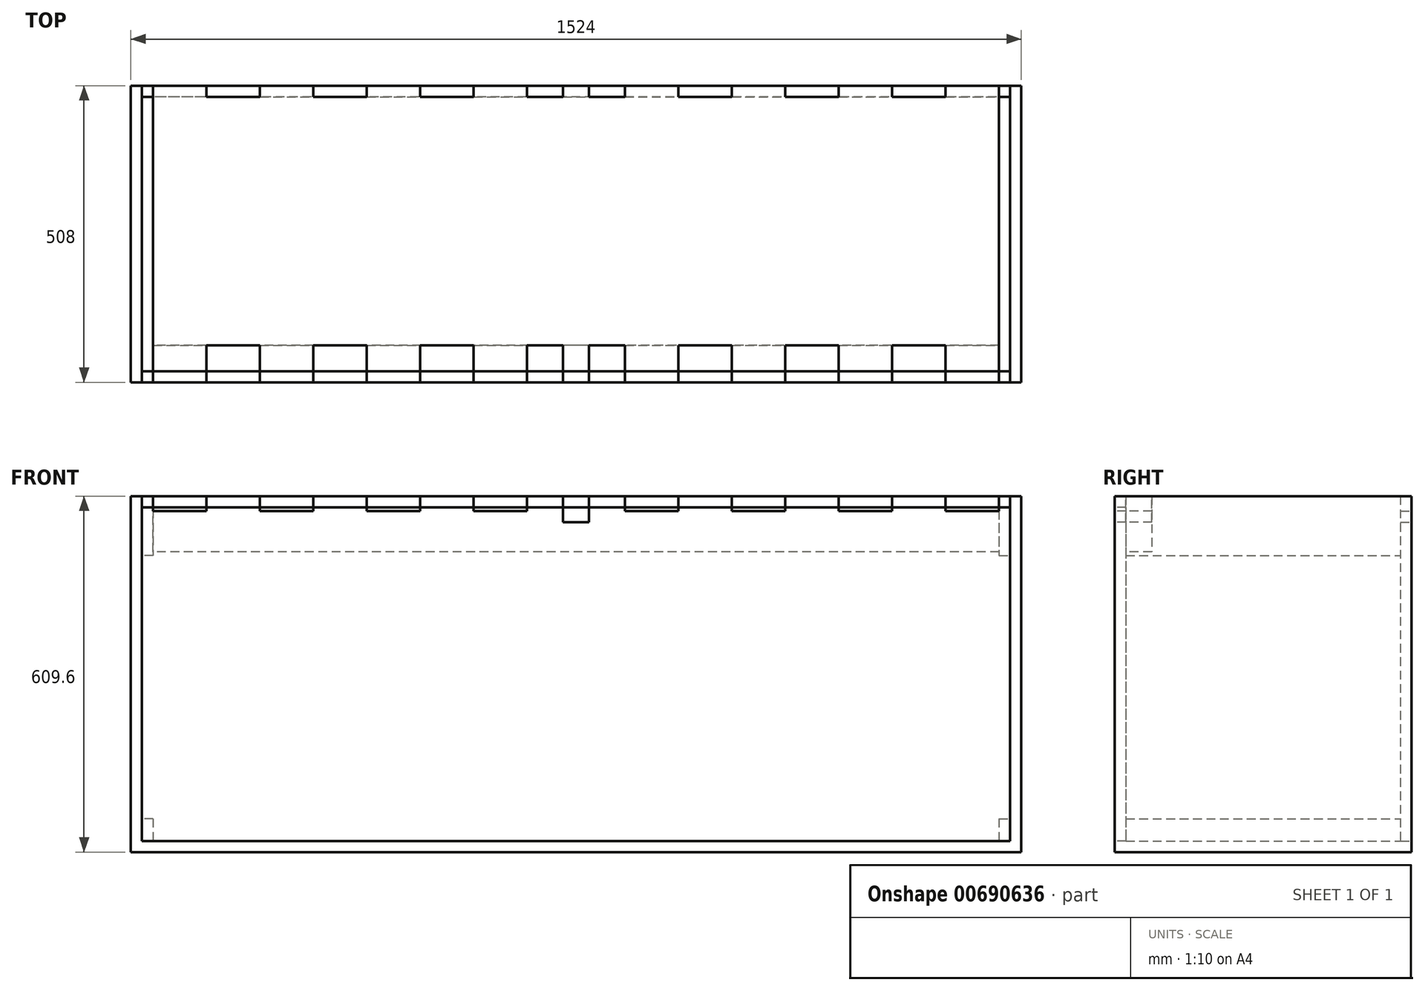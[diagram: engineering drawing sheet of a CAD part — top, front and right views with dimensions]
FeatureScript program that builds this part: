
annotation { "Feature Type Name" : "Feature", "Feature Type Description" : "" }
export const myFeature = defineFeature(function(context is Context, id is Id, definition is map)
    precondition{}
    {
        {
            var Q0;
            Q0=qCreatedBy(makeId("Top.planeOp"),FACE);
            var sketch = newSketch(context, id + "F0", { "sketchPlane" : qUnion([Q0])});
            skLineSegment(sketch, "E0.bottom", {"start": v(-762, -254) * mm, "end": v(762, -254) * mm});
            skLineSegment(sketch, "E0.top", {"start": v(-762, 254) * mm, "end": v(762, 254) * mm});
            skLineSegment(sketch, "E0.left", {"start": v(-762, -254) * mm, "end": v(-762, 254) * mm});
            skLineSegment(sketch, "E0.right", {"start": v(762, -254) * mm, "end": v(762, 254) * mm});
            skPoint(sketch, "E0.middle", {"position": v(0, 0) * mm});
            skSolve(sketch);
        }
        {
            var Q0;
            Q0=makeQuery(id+"F0.imprint","IMPRINT",FACE,{"disambiguationData":[TD([[makeQuery(id+"F0.imprint","IMPRINT",EDGE,{"derivedFrom":sQuery(id+"F0.wireOp",EDGE,"E0.bottom")}),1.0]])]});
            extrude(context, id + "F1", {"entities" : qUnion([Q0]), "oppositeDirection" : true, "depth" : 609.6 * mm, "offsetDistance" : 25.4 * mm});
        }
        {
            var Q0;
            Q0=makeQuery(id+"F1.opExtrude","SWEPT_FACE",FACE,{"disambiguationData":[OSD([sQuery(id+"F0.wireOp",EDGE,"E0.bottom")])]});
            var sketch = newSketch(context, id + "F2", { "sketchPlane" : qUnion([Q0])});
            skLineSegment(sketch, "E1.bottom", {"start": v(-742.95, -19.05) * mm, "end": v(742.95, -19.05) * mm});
            skLineSegment(sketch, "E1.top", {"start": v(-742.95, -590.55) * mm, "end": v(742.95, -590.55) * mm});
            skLineSegment(sketch, "E1.left", {"start": v(-742.95, -19.05) * mm, "end": v(-742.95, -590.55) * mm});
            skLineSegment(sketch, "E1.right", {"start": v(742.95, -19.05) * mm, "end": v(742.95, -590.55) * mm});
            skSolve(sketch);
        }
        {
            var Q0;
            Q0=qSketchRegion(id+"F2",true);
            extrude(context, id + "F3", {"entities" : qUnion([Q0]), "oppositeDirection" : true, "depth" : 19.05 * mm, "offsetDistance" : 25.4 * mm});
        }
        {
            var Q0;
            Q0=makeQuery(id+"F3.opExtrude","CAP_FACE",FACE,{"disambiguationData":[OSD([sQuery(id+"F2.wireOp",EDGE,"E1.bottom"),sQuery(id+"F2.wireOp",EDGE,"E1.top"),sQuery(id+"F2.wireOp",EDGE,"E1.left"),sQuery(id+"F2.wireOp",EDGE,"E1.right")])],"isStart":false});
            var sketch = newSketch(context, id + "F4", { "sketchPlane" : qUnion([Q0])});
            skLineSegment(sketch, "E2", {"start": v(-723.9, -95.25) * mm, "end": v(723.9, -95.25) * mm});
            skLineSegment(sketch, "E3", {"start": v(723.9, -95.25) * mm, "end": v(723.9, -25.4) * mm});
            skLineSegment(sketch, "E4", {"start": v(723.9, -25.4) * mm, "end": v(632.46, -25.4) * mm});
            skLineSegment(sketch, "E5", {"start": v(632.46, -25.4) * mm, "end": v(632.46, 0) * mm});
            skLineSegment(sketch, "E6", {"start": v(632.46, 0) * mm, "end": v(541.02, 0) * mm});
            skLineSegment(sketch, "E7", {"start": v(541.02, 0) * mm, "end": v(541.02, -25.4) * mm});
            skLineSegment(sketch, "E8", {"start": v(541.02, -25.4) * mm, "end": v(449.58, -25.4) * mm});
            skLineSegment(sketch, "E9", {"start": v(449.58, -25.4) * mm, "end": v(449.58, 0) * mm});
            skLineSegment(sketch, "E10", {"start": v(449.58, 0) * mm, "end": v(358.14, 0) * mm});
            skLineSegment(sketch, "E11", {"start": v(358.14, 0) * mm, "end": v(358.14, -25.4) * mm});
            skLineSegment(sketch, "E12", {"start": v(358.14, -25.4) * mm, "end": v(266.7, -25.4) * mm});
            skLineSegment(sketch, "E13", {"start": v(266.7, -25.4) * mm, "end": v(266.7, 0) * mm});
            skLineSegment(sketch, "E14", {"start": v(266.7, 0) * mm, "end": v(175.26, 0) * mm});
            skLineSegment(sketch, "E15", {"start": v(175.26, 0) * mm, "end": v(175.26, -25.4) * mm});
            skLineSegment(sketch, "E16", {"start": v(175.26, -25.4) * mm, "end": v(83.82, -25.4) * mm});
            skLineSegment(sketch, "E17", {"start": v(83.82, -25.4) * mm, "end": v(83.82, 0) * mm});
            skLineSegment(sketch, "E18", {"start": v(-83.82, 0) * mm, "end": v(-83.82, -25.4) * mm});
            skLineSegment(sketch, "E19", {"start": v(-83.82, -25.4) * mm, "end": v(-175.26, -25.4) * mm});
            skLineSegment(sketch, "E20", {"start": v(-175.26, -25.4) * mm, "end": v(-175.26, 0) * mm});
            skLineSegment(sketch, "E21", {"start": v(-175.26, 0) * mm, "end": v(-266.7, 0) * mm});
            skLineSegment(sketch, "E22", {"start": v(-266.7, 0) * mm, "end": v(-266.7, -25.4) * mm});
            skLineSegment(sketch, "E23", {"start": v(-266.7, -25.4) * mm, "end": v(-358.14, -25.4) * mm});
            skLineSegment(sketch, "E24", {"start": v(-358.14, -25.4) * mm, "end": v(-358.14, 0) * mm});
            skLineSegment(sketch, "E25", {"start": v(-358.14, 0) * mm, "end": v(-449.58, 0) * mm});
            skLineSegment(sketch, "E26", {"start": v(-449.58, 0) * mm, "end": v(-449.58, -25.4) * mm});
            skLineSegment(sketch, "E27", {"start": v(-449.58, -25.4) * mm, "end": v(-541.02, -25.4) * mm});
            skLineSegment(sketch, "E28", {"start": v(-541.02, -25.4) * mm, "end": v(-541.02, 0) * mm});
            skLineSegment(sketch, "E29", {"start": v(-541.02, 0) * mm, "end": v(-632.46, 0) * mm});
            skLineSegment(sketch, "E30", {"start": v(-632.46, 0) * mm, "end": v(-632.46, -25.4) * mm});
            skLineSegment(sketch, "E31", {"start": v(-632.46, -25.4) * mm, "end": v(-723.9, -25.4) * mm});
            skLineSegment(sketch, "E32", {"start": v(-723.9, -25.4) * mm, "end": v(-723.9, -95.25) * mm});
            skLineSegment(sketch, "E33", {"start": v(-83.82, 0) * mm, "end": v(-22.22, 0) * mm});
            skLineSegment(sketch, "E34", {"start": v(-22.22, 0) * mm, "end": v(-22.22, -44.45) * mm});
            skLineSegment(sketch, "E35", {"start": v(-22.22, -44.45) * mm, "end": v(22.23, -44.45) * mm});
            skLineSegment(sketch, "E36", {"start": v(22.23, -44.45) * mm, "end": v(22.23, 0) * mm});
            skLineSegment(sketch, "E37", {"start": v(22.23, 0) * mm, "end": v(83.82, 0) * mm});
            skSolve(sketch);
        }
        {
            var Q0;
            Q0=qSketchRegion(id+"F4",true);
            extrude(context, id + "F5", {"entities" : qUnion([Q0]), "depth" : 44.45 * mm, "offsetDistance" : 25.4 * mm});
        }
        {
            var Q0;
            Q0=makeQuery(id+"F1.opExtrude","SWEPT_FACE",FACE,{"disambiguationData":[OSD([sQuery(id+"F0.wireOp",EDGE,"E0.top")])]});
            var sketch = newSketch(context, id + "F6", { "sketchPlane" : qUnion([Q0])});
            skLineSegment(sketch, "E38", {"start": v(-742.95, -590.55) * mm, "end": v(742.95, -590.55) * mm});
            skLineSegment(sketch, "E39", {"start": v(742.95, -590.55) * mm, "end": v(742.95, 0) * mm});
            skLineSegment(sketch, "E40", {"start": v(632.46, -25.4) * mm, "end": v(632.46, 0) * mm});
            skLineSegment(sketch, "E41", {"start": v(632.46, 0) * mm, "end": v(541.02, 0) * mm});
            skLineSegment(sketch, "E42", {"start": v(541.02, 0) * mm, "end": v(541.02, -25.4) * mm});
            skLineSegment(sketch, "E43", {"start": v(541.02, -25.4) * mm, "end": v(449.58, -25.4) * mm});
            skLineSegment(sketch, "E44", {"start": v(449.58, -25.4) * mm, "end": v(449.58, 0) * mm});
            skLineSegment(sketch, "E45", {"start": v(449.58, 0) * mm, "end": v(358.14, 0) * mm});
            skLineSegment(sketch, "E46", {"start": v(358.14, 0) * mm, "end": v(358.14, -25.4) * mm});
            skLineSegment(sketch, "E47", {"start": v(358.14, -25.4) * mm, "end": v(266.7, -25.4) * mm});
            skLineSegment(sketch, "E48", {"start": v(266.7, -25.4) * mm, "end": v(266.7, 0) * mm});
            skLineSegment(sketch, "E49", {"start": v(266.7, 0) * mm, "end": v(175.26, 0) * mm});
            skLineSegment(sketch, "E50", {"start": v(175.26, 0) * mm, "end": v(175.26, -25.4) * mm});
            skLineSegment(sketch, "E51", {"start": v(175.26, -25.4) * mm, "end": v(83.82, -25.4) * mm});
            skLineSegment(sketch, "E52", {"start": v(83.82, -25.4) * mm, "end": v(83.82, 0) * mm});
            skLineSegment(sketch, "E53", {"start": v(83.82, 0) * mm, "end": v(22.23, 0) * mm});
            skLineSegment(sketch, "E54", {"start": v(22.23, 0) * mm, "end": v(22.23, -44.45) * mm});
            skLineSegment(sketch, "E55", {"start": v(22.23, -44.45) * mm, "end": v(-22.22, -44.45) * mm});
            skLineSegment(sketch, "E56", {"start": v(-22.22, -44.45) * mm, "end": v(-22.22, 0) * mm});
            skLineSegment(sketch, "E57", {"start": v(-22.22, 0) * mm, "end": v(-83.82, 0) * mm});
            skLineSegment(sketch, "E58", {"start": v(-83.82, 0) * mm, "end": v(-83.82, -25.4) * mm});
            skLineSegment(sketch, "E59", {"start": v(-83.82, -25.4) * mm, "end": v(-175.26, -25.4) * mm});
            skLineSegment(sketch, "E60", {"start": v(-175.26, -25.4) * mm, "end": v(-175.26, 0) * mm});
            skLineSegment(sketch, "E61", {"start": v(-175.26, 0) * mm, "end": v(-266.7, 0) * mm});
            skLineSegment(sketch, "E62", {"start": v(-266.7, 0) * mm, "end": v(-266.7, -25.4) * mm});
            skLineSegment(sketch, "E63", {"start": v(-266.7, -25.4) * mm, "end": v(-358.14, -25.4) * mm});
            skLineSegment(sketch, "E64", {"start": v(-358.14, -25.4) * mm, "end": v(-358.14, 0) * mm});
            skLineSegment(sketch, "E65", {"start": v(-358.14, 0) * mm, "end": v(-449.58, 0) * mm});
            skLineSegment(sketch, "E66", {"start": v(-449.58, 0) * mm, "end": v(-449.58, -25.4) * mm});
            skLineSegment(sketch, "E67", {"start": v(-449.58, -25.4) * mm, "end": v(-541.02, -25.4) * mm});
            skLineSegment(sketch, "E68", {"start": v(-541.02, -25.4) * mm, "end": v(-541.02, 0) * mm});
            skLineSegment(sketch, "E69", {"start": v(-541.02, 0) * mm, "end": v(-632.46, 0) * mm});
            skLineSegment(sketch, "E70", {"start": v(-632.46, 0) * mm, "end": v(-632.46, -25.4) * mm});
            skLineSegment(sketch, "E71", {"start": v(-742.95, 0) * mm, "end": v(-742.95, -590.55) * mm});
            skLineSegment(sketch, "E72", {"start": v(-632.46, -25.4) * mm, "end": v(-723.9, -25.4) * mm});
            skLineSegment(sketch, "E73", {"start": v(-723.9, -25.4) * mm, "end": v(-723.9, 0) * mm});
            skLineSegment(sketch, "E74", {"start": v(-723.9, 0) * mm, "end": v(-742.95, 0) * mm});
            skLineSegment(sketch, "E75", {"start": v(632.46, -25.4) * mm, "end": v(723.9, -25.4) * mm});
            skLineSegment(sketch, "E76", {"start": v(723.9, -25.4) * mm, "end": v(723.9, 0) * mm});
            skLineSegment(sketch, "E77", {"start": v(723.9, 0) * mm, "end": v(742.95, 0) * mm});
            skSolve(sketch);
        }
        {
            var Q0;
            Q0=qSketchRegion(id+"F6",true);
            extrude(context, id + "F7", {"entities" : qUnion([Q0]), "oppositeDirection" : true, "depth" : 19.05 * mm, "offsetDistance" : 25.4 * mm});
        }
        {
            var Q0;
            Q0=makeQuery(id+"F3.opExtrude","SWEPT_FACE",FACE,{"disambiguationData":[OSD([sQuery(id+"F2.wireOp",EDGE,"E1.right")])]});
            var sketch = newSketch(context, id + "F8", { "sketchPlane" : qUnion([Q0])});
            skLineSegment(sketch, "E78.bottom", {"start": v(-234.95, 0) * mm, "end": v(234.95, 0) * mm});
            skLineSegment(sketch, "E78.top", {"start": v(-234.95, -101.6) * mm, "end": v(234.95, -101.6) * mm});
            skLineSegment(sketch, "E78.left", {"start": v(-234.95, 0) * mm, "end": v(-234.95, -101.6) * mm});
            skLineSegment(sketch, "E78.right", {"start": v(234.95, 0) * mm, "end": v(234.95, -101.6) * mm});
            skLineSegment(sketch, "E79.bottom", {"start": v(-234.95, -552.45) * mm, "end": v(234.95, -552.45) * mm});
            skLineSegment(sketch, "E79.top", {"start": v(-234.95, -590.55) * mm, "end": v(234.95, -590.55) * mm});
            skLineSegment(sketch, "E79.left", {"start": v(-234.95, -552.45) * mm, "end": v(-234.95, -590.55) * mm});
            skLineSegment(sketch, "E79.right", {"start": v(234.95, -552.45) * mm, "end": v(234.95, -590.55) * mm});
            skSolve(sketch);
        }
        {
            var Q0;
            Q0=qSketchRegion(id+"F8",true);
            extrude(context, id + "F9", {"entities" : qUnion([Q0]), "oppositeDirection" : true, "depth" : 19.05 * mm, "offsetDistance" : 25.4 * mm});
        }
        {
            var Q0;
            Q0=makeQuery(id+"F9.opExtrude","SWEPT_BODY",BODY,{"disambiguationData":[OSD([sQuery(id+"F8.wireOp",EDGE,"E78.bottom"),sQuery(id+"F8.wireOp",EDGE,"E78.top"),sQuery(id+"F8.wireOp",EDGE,"E78.left"),sQuery(id+"F8.wireOp",EDGE,"E78.right")])]});
            var Q1;
            Q1=makeQuery(id+"F9.opExtrude","SWEPT_BODY",BODY,{"disambiguationData":[OSD([sQuery(id+"F8.wireOp",EDGE,"E79.bottom"),sQuery(id+"F8.wireOp",EDGE,"E79.top"),sQuery(id+"F8.wireOp",EDGE,"E79.left"),sQuery(id+"F8.wireOp",EDGE,"E79.right")])]});
            var Q2;
            Q2=qCreatedBy(makeId("Right.planeOp"),FACE);
            mirror(context, id + "F10", {"entities" : qUnion([Q0, Q1]), "mirrorPlane" : qUnion([Q2])});
        }
        {
            var Q0;
            Q0=makeQuery(id+"F3.opExtrude","SWEPT_FACE",FACE,{"disambiguationData":[OSD([sQuery(id+"F2.wireOp",EDGE,"E1.bottom")])]});
            var sketch = newSketch(context, id + "F11", { "sketchPlane" : qUnion([Q0])});
            skLineSegment(sketch, "E80.bottom", {"start": v(-742.95, -254) * mm, "end": v(742.95, -254) * mm});
            skLineSegment(sketch, "E80.top", {"start": v(-742.95, -234.95) * mm, "end": v(742.95, -234.95) * mm});
            skLineSegment(sketch, "E80.left", {"start": v(-742.95, -254) * mm, "end": v(-742.95, -234.95) * mm});
            skLineSegment(sketch, "E80.right", {"start": v(742.95, -254) * mm, "end": v(742.95, -234.95) * mm});
            skSolve(sketch);
        }
        {
            var Q0;
            Q0=qSketchRegion(id+"F11",true);
            extrude(context, id + "F12", {"entities" : qUnion([Q0]), "depth" : 19.05 * mm, "offsetDistance" : 25.4 * mm});
        }
        {
            var Q0;
            Q0=makeQuery(id+"F7.opExtrude","SWEPT_BODY",BODY,{"disambiguationData":[OSD([sQuery(id+"F6.wireOp",EDGE,"E38"),sQuery(id+"F6.wireOp",EDGE,"E39"),sQuery(id+"F6.wireOp",EDGE,"E40"),sQuery(id+"F6.wireOp",EDGE,"E41"),sQuery(id+"F6.wireOp",EDGE,"E42"),sQuery(id+"F6.wireOp",EDGE,"E43"),sQuery(id+"F6.wireOp",EDGE,"E44"),sQuery(id+"F6.wireOp",EDGE,"E45"),sQuery(id+"F6.wireOp",EDGE,"E46"),sQuery(id+"F6.wireOp",EDGE,"E47"),sQuery(id+"F6.wireOp",EDGE,"E48"),sQuery(id+"F6.wireOp",EDGE,"E49"),sQuery(id+"F6.wireOp",EDGE,"E50"),sQuery(id+"F6.wireOp",EDGE,"E51"),sQuery(id+"F6.wireOp",EDGE,"E52"),sQuery(id+"F6.wireOp",EDGE,"E53"),sQuery(id+"F6.wireOp",EDGE,"E54"),sQuery(id+"F6.wireOp",EDGE,"E55"),sQuery(id+"F6.wireOp",EDGE,"E56"),sQuery(id+"F6.wireOp",EDGE,"E57"),sQuery(id+"F6.wireOp",EDGE,"E58"),sQuery(id+"F6.wireOp",EDGE,"E59"),sQuery(id+"F6.wireOp",EDGE,"E60"),sQuery(id+"F6.wireOp",EDGE,"E61"),sQuery(id+"F6.wireOp",EDGE,"E62"),sQuery(id+"F6.wireOp",EDGE,"E63"),sQuery(id+"F6.wireOp",EDGE,"E64"),sQuery(id+"F6.wireOp",EDGE,"E65"),sQuery(id+"F6.wireOp",EDGE,"E66"),sQuery(id+"F6.wireOp",EDGE,"E67"),sQuery(id+"F6.wireOp",EDGE,"E68"),sQuery(id+"F6.wireOp",EDGE,"E69"),sQuery(id+"F6.wireOp",EDGE,"E70"),sQuery(id+"F6.wireOp",EDGE,"E71"),sQuery(id+"F6.wireOp",EDGE,"E72"),sQuery(id+"F6.wireOp",EDGE,"E73"),sQuery(id+"F6.wireOp",EDGE,"E74"),sQuery(id+"F6.wireOp",EDGE,"E75"),sQuery(id+"F6.wireOp",EDGE,"E76"),sQuery(id+"F6.wireOp",EDGE,"E77")])]});
            var Q1;
            Q1=qCreatedBy(makeId("Front.planeOp"),FACE);
            mirror(context, id + "F13", {"entities" : qUnion([Q0]), "mirrorPlane" : qUnion([Q1])});
        }
    });
